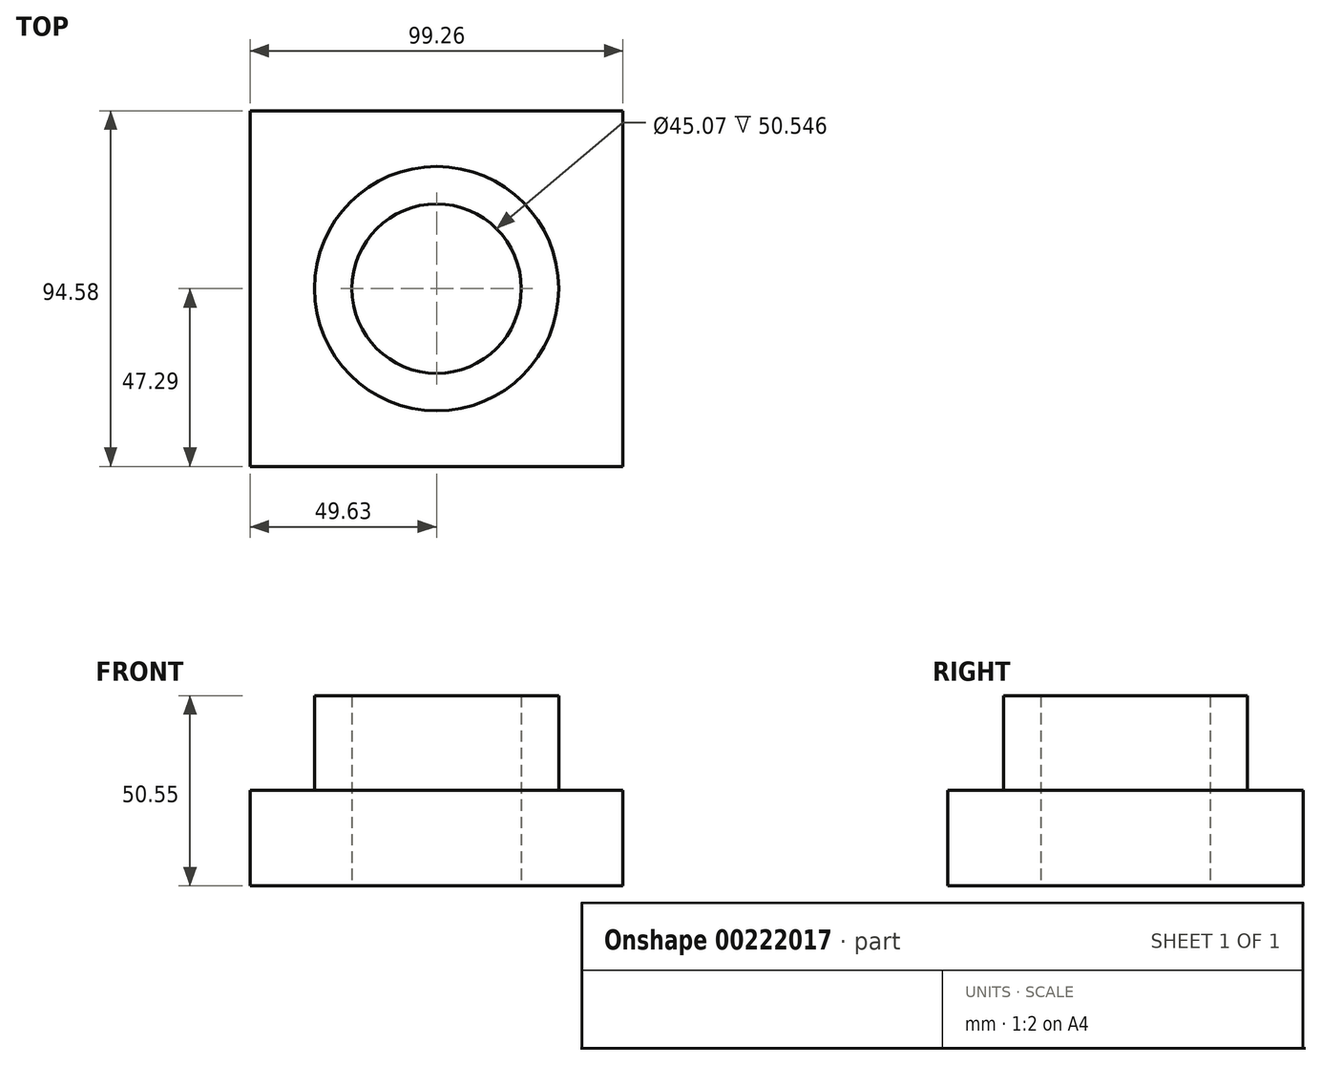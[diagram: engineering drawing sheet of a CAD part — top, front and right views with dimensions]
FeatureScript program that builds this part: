
annotation { "Feature Type Name" : "Feature", "Feature Type Description" : "" }
export const myFeature = defineFeature(function(context is Context, id is Id, definition is map)
    precondition{}
    {
        {
            var Q0;
            Q0=qCreatedBy(makeId("Top.planeOp"),FACE);
            var sketch = newSketch(context, id + "F0", { "sketchPlane" : qUnion([Q0])});
            skLineSegment(sketch, "E0.bottom", {"start": v(49.63, 47.29) * mm, "end": v(-49.63, 47.29) * mm});
            skLineSegment(sketch, "E0.top", {"start": v(49.63, -47.29) * mm, "end": v(-49.63, -47.29) * mm});
            skLineSegment(sketch, "E0.left", {"start": v(49.63, 47.29) * mm, "end": v(49.63, -47.29) * mm});
            skLineSegment(sketch, "E0.right", {"start": v(-49.63, 47.29) * mm, "end": v(-49.63, -47.29) * mm});
            skPoint(sketch, "E0.middle", {"position": v(0, 0) * mm});
            skCircle(sketch, "E1", {"center": v(0, 0) * mm, "radius": 22.53 * mm});
            skCircle(sketch, "E2", {"center": v(0, 0) * mm, "radius": 32.5 * mm});
            skSolve(sketch);
        }
        {
            var Q0;
            Q0=makeQuery(id+"F0.imprint","IMPRINT",FACE,{"disambiguationData":[TD([[makeQuery(id+"F0.imprint","IMPRINT",EDGE,{"derivedFrom":sQuery(id+"F0.wireOp",EDGE,"E1")}),-1.0]])]});
            extrude(context, id + "F1", {"entities" : qUnion([Q0]), "depth" : 50.55 * mm});
        }
        {
            var Q0;
            Q0=makeQuery(id+"F0.imprint","IMPRINT",FACE,{"disambiguationData":[TD([[makeQuery(id+"F0.imprint","IMPRINT",EDGE,{"derivedFrom":sQuery(id+"F0.wireOp",EDGE,"E0.bottom")}),1.0]])]});
            extrude(context, id + "F2", {"entities" : qUnion([Q0]), "operationType" : NewBodyOperationType.ADD, "depth" : 25.4 * mm});
        }
    });
